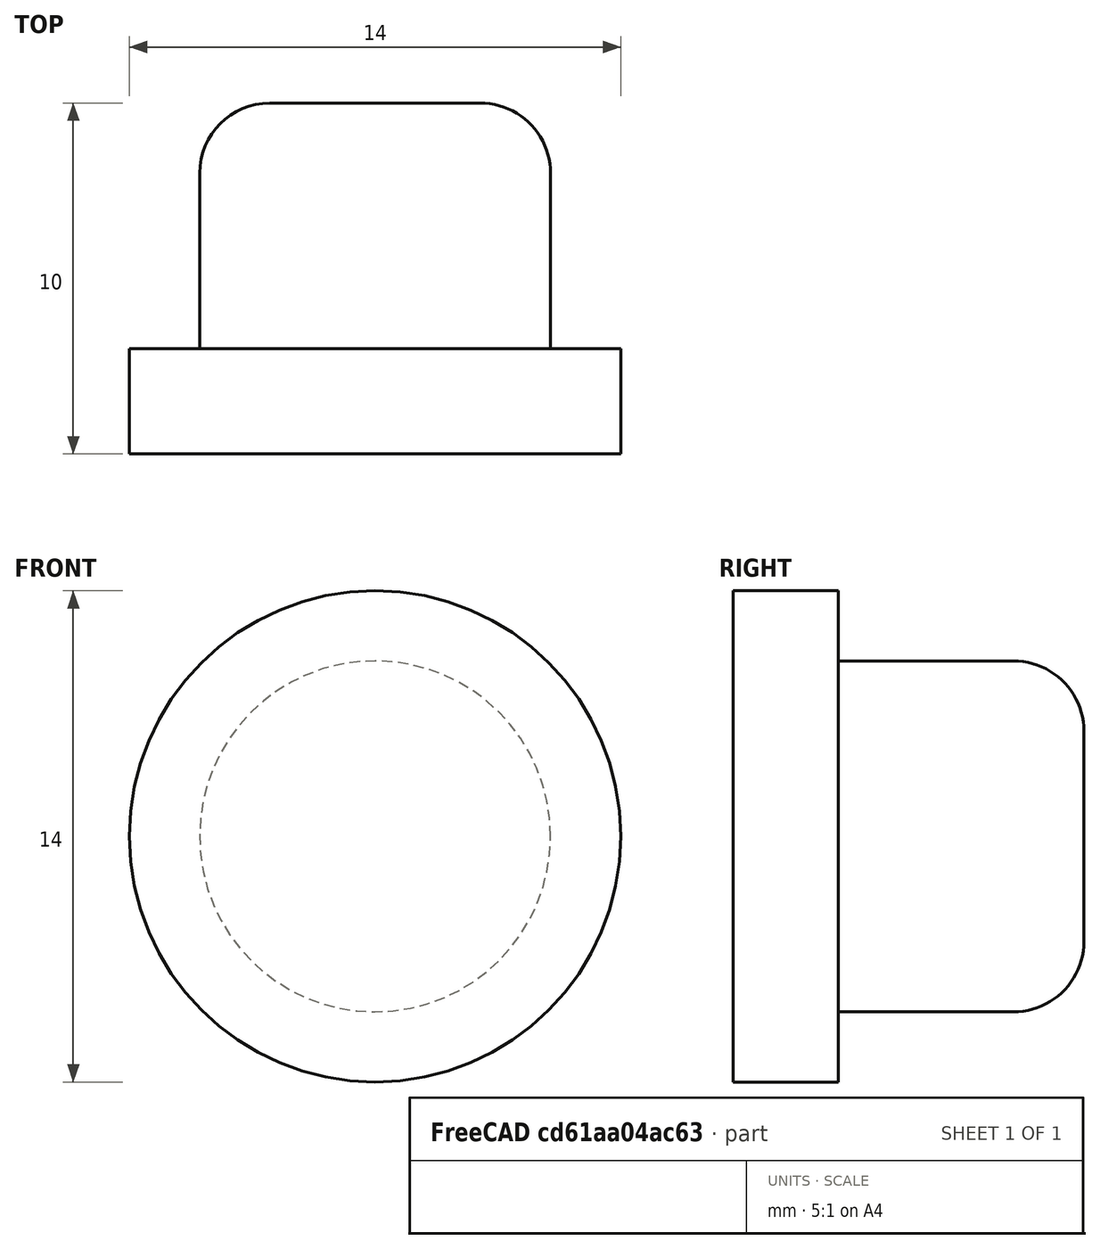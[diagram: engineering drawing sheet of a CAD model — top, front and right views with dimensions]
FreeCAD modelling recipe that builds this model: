
FCSTD DOCUMENT  (FreeCAD 0.18R16093 (Git))
Label: button
License: All rights reserved
LicenseURL: http://en.wikipedia.org/wiki/All_rights_reserved
objects: TechDraw::DrawViewDimension×7, TechDraw::DrawViewPart×3, Sketcher::SketchObject×2, PartDesign::Pad×1, PartDesign::Pocket×1, PartDesign::Fillet×1, PartDesign::Body×1, TechDraw::DrawSVGTemplate×1, TechDraw::DrawPage×1
note: 8 computed .brp shape members not serialized (recipe doc carries the construction recipe); baked Part::Feature solids carry a one-line shape summary decoded from their .brp

FEATURE [Sketcher::SketchObject] Sketch
  MapMode = 5
  Placement = pos=(0,0,0) rot=(1,0,0;1.5708rad)
  Support = -> [XZ_Plane]
  sketch-geometry (1):
    g0: Circle CenterX=0 CenterY=0 CenterZ=0 NormalX=0 NormalY=0 NormalZ=1 AngleXU=0 Radius=7
  constraints (2):
    c: Coincident(g0,g-1)
    c: Radius(g0) = 7
FEATURE [PartDesign::Pad] Pad
  Length = 10
  Length2 = 100
  Placement = pos=(0,0,0) rot=(1,0,0;1.5708rad)
  Profile = -> Sketch
  Type = 0
FEATURE [Sketcher::SketchObject] Sketch001
  MapMode = 5
  Placement = pos=(0,-10,4.4e-15) rot=(1,0,0;1.5708rad)
  Support = -> [Pad]
  sketch-geometry (2):
    g0: Circle CenterX=0 CenterY=0 CenterZ=0 NormalX=0 NormalY=0 NormalZ=1 AngleXU=0 Radius=5
    g1: Circle CenterX=0 CenterY=0 CenterZ=0 NormalX=0 NormalY=0 NormalZ=1 AngleXU=0 Radius=7
  constraints (4):
    c: Coincident(g0,g-1)
    c: Radius(g0) = 5
    c: Coincident(g1,g-1)
    c: Radius(g1) = 7
FEATURE [PartDesign::Pocket] Pocket
  BaseFeature = -> Pad
  Length = 7
  Length2 = 100
  Placement = pos=(0,0,0) rot=(1,0,0;1.5708rad)
  Profile = -> Sketch001
  Type = 0
FEATURE [PartDesign::Fillet] Fillet
  Base = -> Pocket [Edge6]
  BaseFeature = -> Pocket
  Placement = pos=(0,0,0) rot=(1,0,0;1.5708rad)
  Radius = 2
FEATURE [PartDesign::Body] Body
  Group = -> [Sketch,Pad,Sketch001,Pocket,Fillet]
  Origin = -> Origin
  Placement = pos=(0,0,0) rot=(0,0,1;3.14159rad)
  Tip = -> Fillet
FEATURE [TechDraw::DrawSVGTemplate] Template
  EditableTexts = Designed_by_Name=Andreas Renggli; Drawing_number=-; FC-Date=05.12.2018; FC-SC=1:1; FC-SH=-; FC-Title=MusicBox; Subtitle=Button; Weight=-
  Height = 210
  Orientation = 1
  Width = 297
FEATURE [TechDraw::DrawViewPart] View  label="Side"
  CoarseView = false
  Direction = (0,0,1)
  Focus = 100
  HardHidden = false
  IsoCount = 0
  IsoHidden = false
  IsoVisible = false
  LockPosition = false
  Perspective = false
  Rotation = 0
  ScaleType = 0
  SeamHidden = false
  SeamVisible = false
  SmoothHidden = false
  SmoothVisible = false
  Source = -> [Body]
  X = 140
  Y = 99.1466
FEATURE [TechDraw::DrawViewPart] View001  label="3D"
  CoarseView = false
  Direction = (-1,1,-1)
  Focus = 100
  HardHidden = false
  IsoCount = 0
  IsoHidden = false
  IsoVisible = false
  LockPosition = false
  Perspective = false
  Rotation = 0
  ScaleType = 0
  SeamHidden = false
  SeamVisible = false
  SmoothHidden = false
  SmoothVisible = false
  Source = -> [Body]
  X = 90
  Y = 100
FEATURE [TechDraw::DrawViewPart] View002  label="Top"
  CoarseView = false
  Direction = (0,1,0)
  Focus = 100
  HardHidden = false
  IsoCount = 0
  IsoHidden = false
  IsoVisible = false
  LockPosition = false
  Perspective = false
  Rotation = 0
  ScaleType = 0
  SeamHidden = false
  SeamVisible = false
  SmoothHidden = false
  SmoothVisible = false
  Source = -> [Body]
  X = 189.829
  Y = 99.8293
FEATURE [TechDraw::DrawViewDimension] Dimension
  Arbitrary = false
  FormatSpec = %.2f
  LockPosition = false
  MeasureType = 1
  OverTolerance = 0
  References2D = -> [View002]
  Rotation = 0
  ScaleType = 0
  Type = 5
  UnderTolerance = 0
  X = 29.5988
  Y = 10.5969
FEATURE [TechDraw::DrawViewDimension] Dimension002
  Arbitrary = false
  FormatSpec = %.2f
  LockPosition = false
  MeasureType = 1
  OverTolerance = 0
  References2D = -> [View]
  Rotation = 0
  ScaleType = 0
  Type = 0
  UnderTolerance = 0
  X = 20.5784
  Y = 18.8129
FEATURE [TechDraw::DrawViewDimension] Dimension003
  Arbitrary = false
  FormatSpec = %.2f
  LockPosition = false
  MeasureType = 1
  OverTolerance = 0
  References2D = -> [View]
  Rotation = 0
  ScaleType = 0
  Type = 5
  UnderTolerance = 0
  X = -28.6675
  Y = 18.0417
FEATURE [TechDraw::DrawViewDimension] Dimension004
  Arbitrary = false
  FormatSpec = %.2f
  LockPosition = false
  MeasureType = 1
  OverTolerance = 0
  References2D = -> [View]
  Rotation = 0
  ScaleType = 0
  Type = 0
  UnderTolerance = 0
  X = -25.9008
  Y = -13.9235
FEATURE [TechDraw::DrawViewDimension] Dimension005
  Arbitrary = false
  FormatSpec = %.2f
  LockPosition = false
  MeasureType = 1
  OverTolerance = 0
  References2D = -> [View]
  Rotation = 0
  ScaleType = 0
  Type = 2
  UnderTolerance = 0
  X = 11.2706
  Y = 17.9077
FEATURE [TechDraw::DrawViewDimension] Dimension006
  Arbitrary = false
  FormatSpec = %.2f
  LockPosition = false
  MeasureType = 1
  OverTolerance = 0
  References2D = -> [View]
  Rotation = 0
  ScaleType = 0
  Type = 0
  UnderTolerance = 0
  X = 22.0172
  Y = 32.5991
FEATURE [TechDraw::DrawViewDimension] Dimension007
  Arbitrary = false
  FormatSpec = %.2f
  LockPosition = false
  MeasureType = 1
  OverTolerance = 0
  References2D = -> [View002]
  Rotation = 0
  ScaleType = 0
  Type = 5
  UnderTolerance = 0
  X = 30.8923
  Y = -9.89919
FEATURE [TechDraw::DrawPage] Page
  KeepUpdated = true
  ProjectionType = 0
  Template = -> Template
  Views = -> [View,View001,View002,Dimension,Dimension002,Dimension003,Dimension004,Dimension005,Dimension006,Dimension007]
